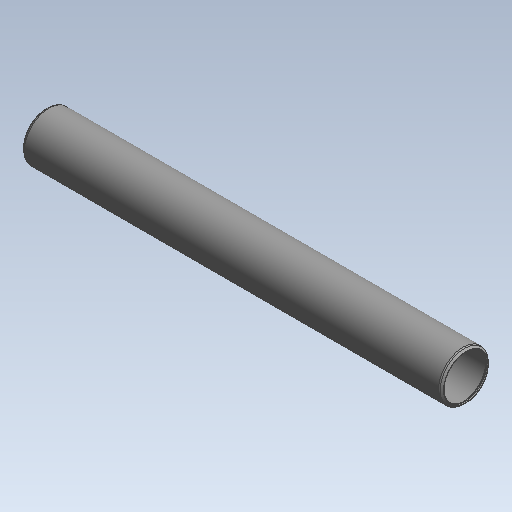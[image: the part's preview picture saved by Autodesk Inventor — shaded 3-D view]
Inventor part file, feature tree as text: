
AUTODESK INVENTOR PART (.ipt)
format: ipt  version: 2020 (Build 240168000, 168)  size: 135,680 bytes
history: native  units: mm (DEFAULTED — no unit token found)
features: other x42, sketch x2, revolve x1, extrude x1
ambient origin geometry x8: Origin, YZ Plane, XZ Plane, XY Plane, X Axis, Y Axis, Z Axis, Center Point
bodies: Solid1 (feature_tree)
feature tree (46):
  revolve  "Revolution1"  [1 undecoded]
  extrude  "Extrusion1"  [1 undecoded]
  other  "cp1_XY"
  other  "cp1_YZ"
  other  "cp1_ZX"
  other  "cp1_X"
  other  "cp1_Y"
  other  "cp1_Z"
  other  "cp1_Center"
  other  "cp2_XY"
  other  "cp2_YZ"
  other  "cp2_ZX"
  other  "cp2_X"
  other  "cp2_Y"
  other  "cp2_Z"
  other  "cp2_Center"
  other  "cp3_XY"
  other  "cp3_YZ"
  other  "cp3_ZX"
  other  "cp3_X"
  other  "cp3_Y"
  other  "cp3_Z"
  other  "cp3_Center"
  other  "cp4_XY"
  other  "cp4_YZ"
  other  "cp4_ZX"
  other  "cp4_X"
  other  "cp4_Y"
  other  "cp4_Z"
  other  "cp4_Center"
  other  "tube_front_XY"
  other  "tube_front_YZ"
  other  "tube_front_ZX"
  other  "tube_front_X"
  other  "tube_front_Y"
  other  "tube_front_Z"
  other  "tube_front_Center"
  other  "tube_rear_XY"
  other  "tube_rear_YZ"
  other  "tube_rear_ZX"
  other  "tube_rear_X"
  other  "tube_rear_Y"
  other  "tube_rear_Z"
  other  "tube_rear_Center"
  sketch  "Sketch_1"  dims[d0=360.0deg d1=10.25525mm d2=0.0mm]
  sketch  "Sketch_7"
note: 2 required parameter values undecoded (feature->parameter linkage not recoverable at this tier; creation-order binding heuristic only, values carry confidence <= 0.55)